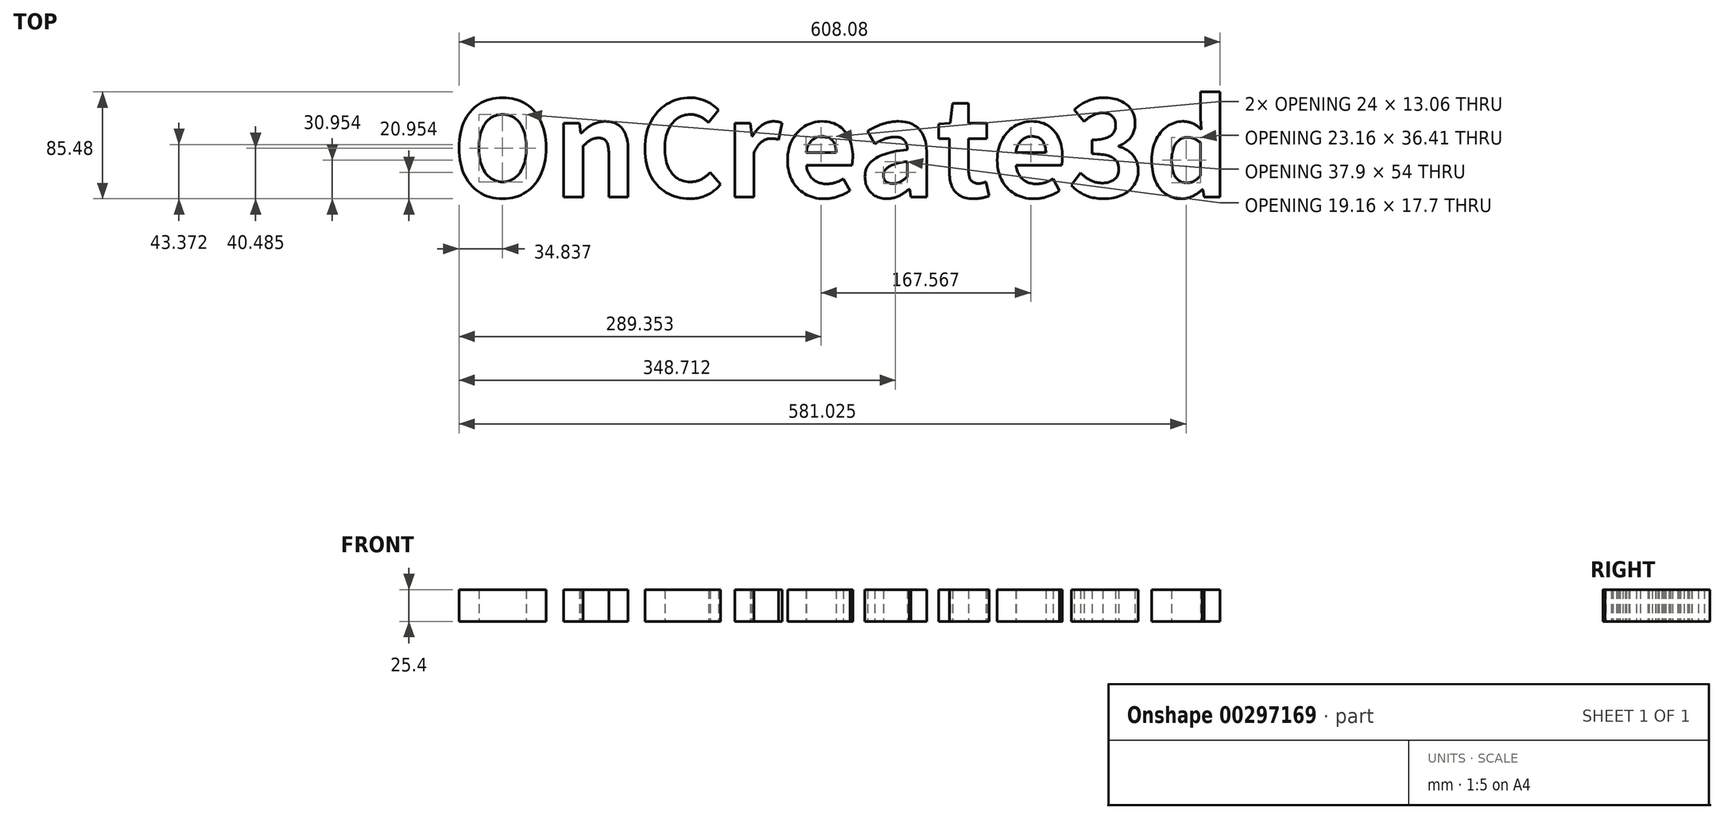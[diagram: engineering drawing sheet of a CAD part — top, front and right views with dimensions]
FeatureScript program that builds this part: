
annotation { "Feature Type Name" : "Feature", "Feature Type Description" : "" }
export const myFeature = defineFeature(function(context is Context, id is Id, definition is map)
    precondition{}
    {
        {
            var Q0;
            Q0=qCreatedBy(makeId("Top.planeOp"),FACE);
            var sketch = newSketch(context, id + "F0", { "sketchPlane" : qUnion([Q0])});
            skText(sketch, "E0", { "text": "OnCreate3d", "fontName": "NotoSansCJKkr-Bold.otf"});
            const initialGuessF0  = {"E0": [-0.25249, -0.0002, 1, 0, 0.07579]};
            skSetInitialGuess(sketch, initialGuessF0);
            skSolve(sketch);
        }
        {
            var Q0;
            Q0 = qSketchRegion(id + "F0", true);
            extrude(context, id + "F1", {"entities" : qUnion([Q0]), "depth" : 25.4 * mm});
        }
    });
